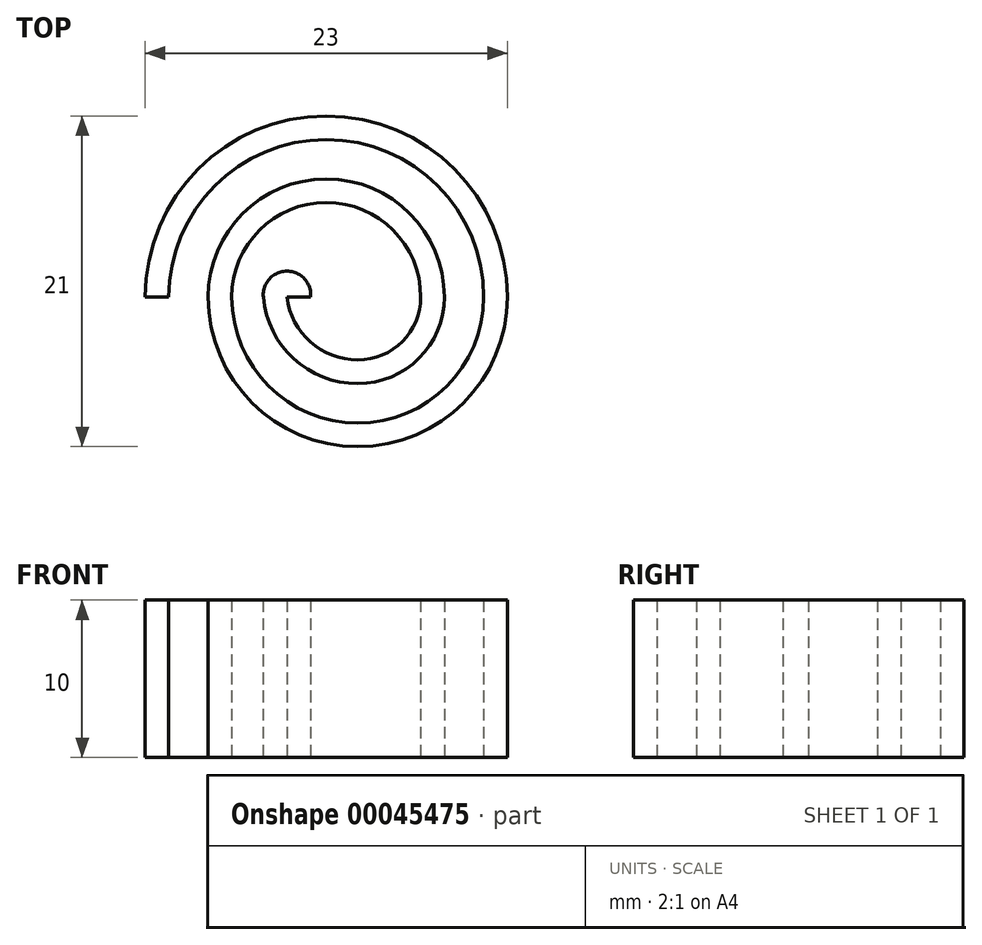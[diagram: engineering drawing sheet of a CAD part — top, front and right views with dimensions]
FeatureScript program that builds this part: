
annotation { "Feature Type Name" : "Feature", "Feature Type Description" : "" }
export const myFeature = defineFeature(function(context is Context, id is Id, definition is map)
    precondition{}
    {
        {
            var Q0;
            Q0=qCreatedBy(makeId("Top.planeOp"),FACE);
            var sketch = newSketch(context, id + "F0", { "sketchPlane" : qUnion([Q0])});
            skLineSegment(sketch, "E0", {"start": v(0, 0) * mm, "end": v(4, 0) * mm, "construction": true});
            skLineSegment(sketch, "E1", {"start": v(0, 0) * mm, "end": v(-2, 0) * mm, "construction": true});
            skArc(sketch, "E2", {"start": v(4, 0) * mm, "mid": v(2.9, 3.46) * mm, "end": v(0, 5.66) * mm});
            skArc(sketch, "E3", {"start": v(0, 5.66) * mm, "mid": v(-5.46, 4.9) * mm, "end": v(-8, 0) * mm});
            skArc(sketch, "E4", {"start": v(-8, 0) * mm, "mid": v(0, -8) * mm, "end": v(8, 0) * mm});
            skArc(sketch, "E5", {"start": v(8, 0) * mm, "mid": v(-2, 10) * mm, "end": v(-12, 0) * mm});
            skArc(sketch, "E6.0", {"start": v(9.5, 0) * mm, "mid": v(-2, 11.5) * mm, "end": v(-13.5, 0) * mm});
            skArc(sketch, "E6.1", {"start": v(-9.5, 0) * mm, "mid": v(0, -9.5) * mm, "end": v(9.5, 0) * mm});
            skArc(sketch, "E6.2", {"start": v(0.5, 7.07) * mm, "mid": v(-6.33, 6.12) * mm, "end": v(-9.5, 0) * mm});
            skArc(sketch, "E6.3", {"start": v(5.5, 0) * mm, "mid": v(4.12, 4.33) * mm, "end": v(0.5, 7.07) * mm});
            skLineSegment(sketch, "E7", {"start": v(-13.5, 0) * mm, "end": v(-12, 0) * mm});
            skArc(sketch, "E8", {"start": v(5.5, 0) * mm, "mid": v(3.89, -3.89) * mm, "end": v(0, -5.5) * mm});
            skArc(sketch, "E9", {"start": v(0, -5.5) * mm, "mid": v(-4.07, -3.92) * mm, "end": v(-6, 0) * mm});
            skArc(sketch, "E10.0", {"start": v(0, -4) * mm, "mid": v(-3, -2.86) * mm, "end": v(-4.5, 0) * mm});
            skArc(sketch, "E10.1", {"start": v(4, 0) * mm, "mid": v(2.83, -2.83) * mm, "end": v(0, -4) * mm});
            skArc(sketch, "E11", {"start": v(-6, 0) * mm, "mid": v(-4.5, 1.64) * mm, "end": v(-3, 0) * mm});
            skLineSegment(sketch, "E12", {"start": v(-4.5, 0) * mm, "end": v(-3, 0) * mm});
            skSolve(sketch);
        }
        {
            var Q0;
            Q0=makeQuery(id+"F0.imprint","IMPRINT",FACE,{"disambiguationData":[TD([[makeQuery(id+"F0.imprint","IMPRINT",EDGE,{"derivedFrom":sQuery(id+"F0.wireOp",EDGE,"E2")}),-1.0]])]});
            extrude(context, id + "F1", {"entities" : qUnion([Q0]), "depth" : 10 * mm});
        }
    });
